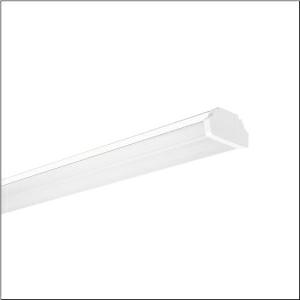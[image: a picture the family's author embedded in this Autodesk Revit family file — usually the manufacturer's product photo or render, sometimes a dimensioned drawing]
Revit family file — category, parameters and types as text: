
# Revit family: dus_31_gen_2_53bd811dv4d5d2_75d9
name_source: partatom
category: Lighting Fixtures
units: mm (PartAtom-declared; Revit-internal decimal feet)

## family parameters
Cut with Voids When Loaded = No
Host = Face
Light Source = No
Part Type = Normal
Room Calculation Point = No
Round Connector Dimension = Use Diameter
Shared = No

## types (1)
- --- (1 x LED, 13680 lm, 74.9 W, 4000K)
    Apparent Load = 75 VA
    CIE Flux Codes = 50 78 94 90 100
    Color Rendering = 80
    Color Temperature = 4000K
    Default Elevation = 1800 mm
    Description = DUS 31 Gen.2, luminaire insert, of sheet steel, coil coated, white, length: 1.535mm, width: 81mm, height: 90mm, 5x system unit, system units: 307mm, LED rated luminous flux: 13.680lm, light colour: 840, SDCM (Standard Deviation of Colour Matching)MacAdam ≤ 3 SDCM (initial), control gear: DALI 2, control gear: ECG DALI, with plug, 5-pole, with phase selection, mains connection: 220..240V, AC, 50/60Hz, rated input power: 75W, through-wiring accessed according to module size, primary optical cover: cover, of PMMA, light emission: direct distribution, primary light characteristic: symmetric, protection rating (complete): IP20, protection rating (LED compartment): IP50, insulation class (complete): insulation class I (protective earthing), certification: CE, ENEC, VDE, UKCA, impact resistance: IK03, permissible ambient temperature for indoor applications: -25..+35°C, corresponds to IFS (International Featured Standards) requirements for safety and quality in the food industry, reducing of maximum allowable ambient temperature of 5°C with ceiling mounting, packaging unit: 1 piece
    Height = 95 mm
    Lamp = 1 x LED
    Lamp Light Flux = 13680 lm
    Lamp Power = 74.9 W
    Lamp count = 1
    Length = 1535 mm
    Luminous efficacy = 183 lm/W
    Manufacturer = Siteco
    ModVariant = No
    Model = 53BD811DV4D5D2
    Mounting Place = Ceiling
    Mounting Type = Pendant
    Number of Poles = 1
    OnlyDefault = Yes
    Power Factor = 1
    Product Name = DUS 31 Gen.2
    Product group = luminaire insert | ceiling pendant
    ProductGroupID = 901
    Protection Class = Protection class I
    Protection Degree = IP 20
    RLX_Detail_Level = 1
    RLX_Emergency_Light_Flux = 0 lm
    RLX_Emergency_Type = 0
    RLX_Emergency_Type_DB = No
    RlxData = <blob elided: 32301 chars, md5=cd3e5ecf>
    Socket = socket
    Standby Power = 0 W
    System Light Flux = 13680 lm
    System Power = 75 W
    Type Comments = factory setting: luminous flux: 100 % | dim-lin: 254 | 511 mA
    Type Image = l_1319596.jpg
    URL = http://relux.com
    VarID = @adj_051741
    Voltage = 0 V
    Weight = 0.00 kg
    Width = 81 mm

## geometry (parser evidence)
native form markers: Blend x4, Sweep x12
no freeform markers — native parametric forms only
